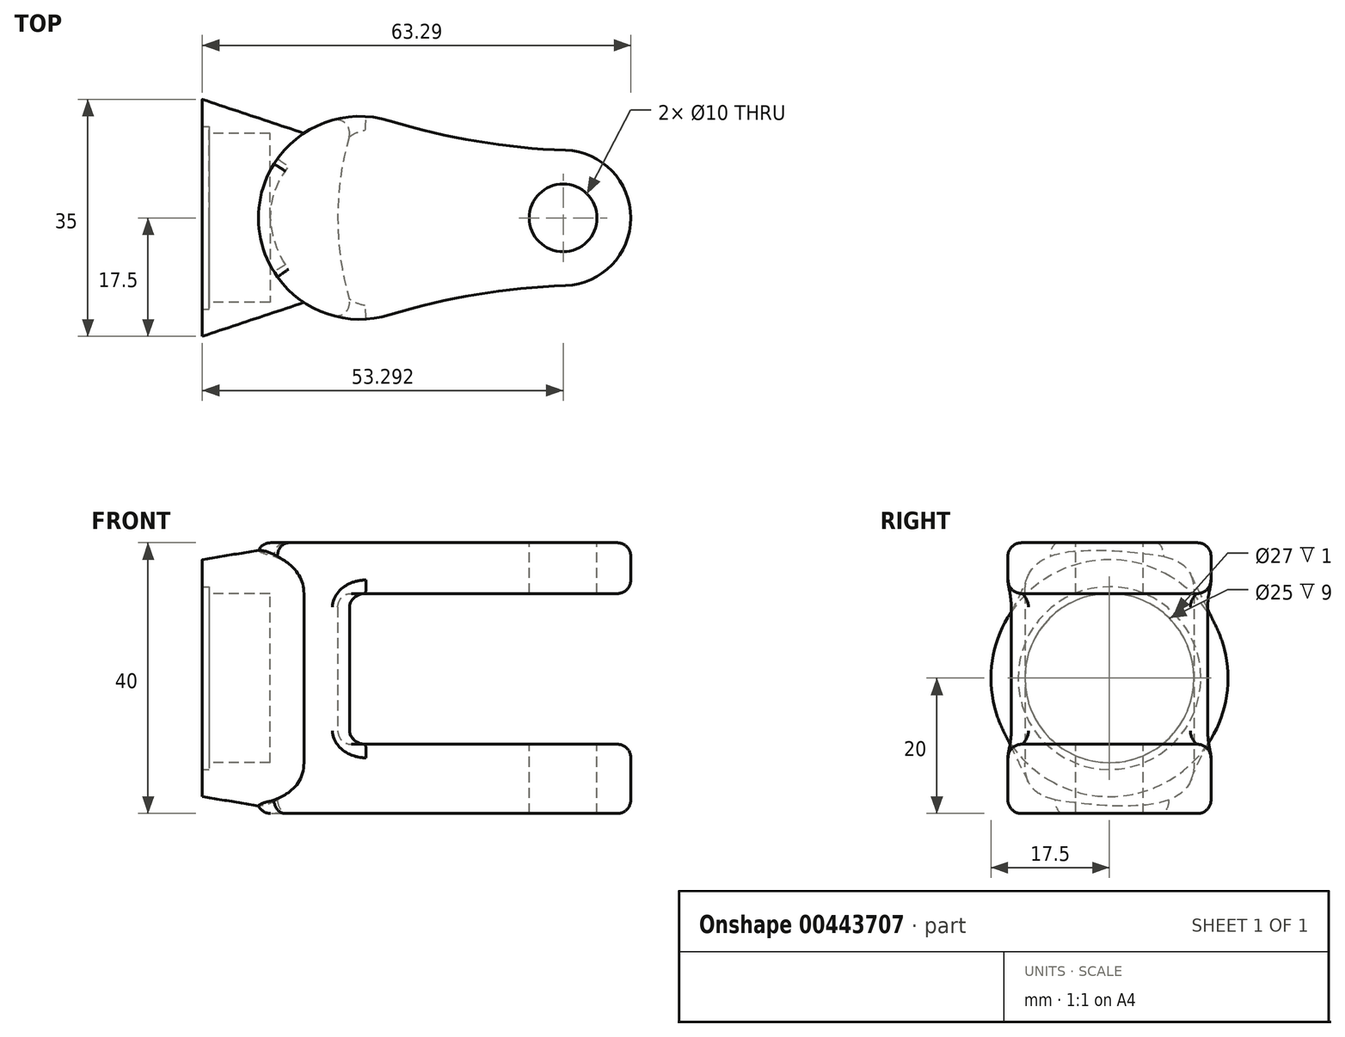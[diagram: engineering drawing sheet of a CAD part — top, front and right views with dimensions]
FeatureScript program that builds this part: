
annotation { "Feature Type Name" : "Feature", "Feature Type Description" : "" }
export const myFeature = defineFeature(function(context is Context, id is Id, definition is map)
    precondition{}
    {
        {
            var Q0;
            Q0=qCreatedBy(makeId("Right.planeOp"),FACE);
            var sketch = newSketch(context, id + "F0", { "sketchPlane" : qUnion([Q0])});
            skCircle(sketch, "E0", {"center": v(0, 0) * mm, "radius": 17.5 * mm});
            skSolve(sketch);
        }
        {
            var Q0;
            Q0=qCreatedBy(makeId("Right.planeOp"),FACE);
            cPlane(context, id + "F1", {"entities" : qUnion([Q0]), "cplaneType" : CPlaneType.OFFSET, "offset" : 15 * mm, "width" : 150 * mm, "height" : 150 * mm});
        }
        {
            var Q0;
            Q0=qCreatedBy(id+"F1.planeOp",FACE);
            var sketch = newSketch(context, id + "F2", { "sketchPlane" : qUnion([Q0])});
            skLineSegment(sketch, "E1.bottom", {"start": v(-5, 20) * mm, "end": v(5, 20) * mm});
            skLineSegment(sketch, "E1.top", {"start": v(-5, -20) * mm, "end": v(5, -20) * mm});
            skLineSegment(sketch, "E1.left", {"start": v(-12.5, 12.5) * mm, "end": v(-12.5, -12.5) * mm});
            skLineSegment(sketch, "E1.right", {"start": v(12.5, 12.5) * mm, "end": v(12.5, -12.5) * mm});
            skPoint(sketch, "E1.middle", {"position": v(0, 0) * mm});
            skPoint(sketch, "E2.visualSharp", {"position": v(-12.5, 20) * mm});
            skArc(sketch, "E2.filletArc", {"start": v(-5, 20) * mm, "mid": v(-10.3, 17.8) * mm, "end": v(-12.5, 12.5) * mm});
            skPoint(sketch, "E3.visualSharp", {"position": v(12.5, 20) * mm});
            skArc(sketch, "E3.filletArc", {"start": v(12.5, 12.5) * mm, "mid": v(10.3, 17.8) * mm, "end": v(5, 20) * mm});
            skPoint(sketch, "E4.visualSharp", {"position": v(-12.5, -20) * mm});
            skArc(sketch, "E4.filletArc", {"start": v(-12.5, -12.5) * mm, "mid": v(-10.3, -17.8) * mm, "end": v(-5, -20) * mm});
            skPoint(sketch, "E5.visualSharp", {"position": v(12.5, -20) * mm});
            skArc(sketch, "E5.filletArc", {"start": v(5, -20) * mm, "mid": v(10.3, -17.8) * mm, "end": v(12.5, -12.5) * mm});
            skSolve(sketch);
        }
        {
            var Q0;
            Q0=makeQuery(id+"F0.imprint","IMPRINT",FACE,{"disambiguationData":[TD([[makeQuery(id+"F0.imprint","IMPRINT",EDGE,{"derivedFrom":sQuery(id+"F0.wireOp",EDGE,"E0")}),1.0]])]});
            var Q1;
            Q1=makeQuery(id+"F2.imprint","IMPRINT",FACE,{"disambiguationData":[TD([[makeQuery(id+"F2.imprint","IMPRINT",EDGE,{"derivedFrom":sQuery(id+"F2.wireOp",EDGE,"E1.bottom")}),-1.0]])]});
            loft(context, id + "F3", {"sheetProfilesArray" : [{ "sheetProfileEntities" : qUnion([Q0]) }, { "sheetProfileEntities" : qUnion([Q1]) }]});
        }
        {
            var Q0;
            Q0=qCreatedBy(makeId("Top.planeOp"),FACE);
            var sketch = newSketch(context, id + "F4", { "sketchPlane" : qUnion([Q0])});
            skArc(sketch, "E6", {"start": v(27.7, 14.34) * mm, "mid": v(8.3, 0) * mm, "end": v(27.7, -14.34) * mm});
            skArc(sketch, "E7", {"start": v(53.63, -10) * mm, "mid": v(63.3, 0) * mm, "end": v(53.63, 10) * mm});
            skLineSegment(sketch, "E8", {"start": v(23.3, 0) * mm, "end": v(53.3, 0) * mm, "construction": true});
            skArc(sketch, "E9", {"start": v(53.63, -10) * mm, "mid": v(40.52, -11.31) * mm, "end": v(27.7, -14.34) * mm});
            skArc(sketch, "E10", {"start": v(27.7, 14.34) * mm, "mid": v(40.52, 11.31) * mm, "end": v(53.63, 10) * mm});
            skSolve(sketch);
        }
        {
            var Q0;
            Q0=makeQuery(id+"F4.imprint","IMPRINT",FACE,{"disambiguationData":[TD([[makeQuery(id+"F4.imprint","IMPRINT",EDGE,{"derivedFrom":sQuery(id+"F4.wireOp",EDGE,"E6")}),1.0]])]});
            extrude(context, id + "F5", {"entities" : qUnion([Q0]), "operationType" : NewBodyOperationType.ADD, "endBound" : BoundingType.SYMMETRIC, "depth" : 40 * mm});
        }
        {
            var Q0;
            Q0=qCreatedBy(makeId("Front.planeOp"),FACE);
            var sketch = newSketch(context, id + "F6", { "sketchPlane" : qUnion([Q0])});
            skLineSegment(sketch, "E11.bottom", {"start": v(20, 12.5) * mm, "end": v(63.63, 12.5) * mm});
            skLineSegment(sketch, "E11.top", {"start": v(20, -9.77) * mm, "end": v(63.63, -9.77) * mm});
            skLineSegment(sketch, "E11.left", {"start": v(20, 12.5) * mm, "end": v(20, -9.77) * mm});
            skLineSegment(sketch, "E11.right", {"start": v(63.63, 12.5) * mm, "end": v(63.63, -9.77) * mm});
            skSolve(sketch);
        }
        {
            var Q0;
            Q0 = qSketchRegion(id + "F6", true);
            var Q1;
            Q1=sQuery(id+"F6.wireOp",EDGE,"E11.right");
            revolve(context, id + "F7", {"operationType" : NewBodyOperationType.REMOVE, "entities" : qUnion([Q0]), "axis" : qUnion([Q1]), "revolveType" : RevolveType.FULL, "oppositeDirection" : true});
        }
        {
            var Q0;
            Q0=qCreatedBy(makeId("Right.planeOp"),FACE);
            var sketch = newSketch(context, id + "F8", { "sketchPlane" : qUnion([Q0])});
            skCircle(sketch, "E12", {"center": v(0, 0) * mm, "radius": 12.5 * mm});
            skSolve(sketch);
        }
        {
            var Q0;
            Q0 = qSketchRegion(id + "F8", true);
            extrude(context, id + "F9", {"entities" : qUnion([Q0]), "operationType" : NewBodyOperationType.REMOVE, "depth" : 10 * mm});
        }
        {
            var Q0;
            Q0=makeQuery(id+"F3.opLoft","CAP_FACE",FACE,{"disambiguationData":[OSD([makeQuery(id+"F0.imprint","IMPRINT",FACE,{"disambiguationData":[TD([[makeQuery(id+"F0.imprint","IMPRINT",EDGE,{"derivedFrom":sQuery(id+"F0.wireOp",EDGE,"E0")}),1.0]])]})])],"isStart":true});
            cPlane(context, id + "F10", {"entities" : qUnion([Q0]), "cplaneType" : CPlaneType.OFFSET, "offset" : 1 * mm, "oppositeDirection" : true, "width" : 150 * mm, "height" : 150 * mm});
        }
        {
            var Q0;
            Q0=qCreatedBy(id+"F10.planeOp",FACE);
            var sketch = newSketch(context, id + "F11", { "sketchPlane" : qUnion([Q0])});
            skCircle(sketch, "E13.0", {"center": v(0, 0) * mm, "radius": 13.5 * mm});
            skSolve(sketch);
        }
        {
            var Q0;
            Q0=makeQuery(id+"F11.imprint","IMPRINT",FACE,{"disambiguationData":[TD([[makeQuery(id+"F11.imprint","IMPRINT",EDGE,{"derivedFrom":sQuery(id+"F11.wireOp",EDGE,"E13.0")}),1.0]])]});
            var Q1;
            Q1=sQuery(id+"F11.wireOp",EDGE,"E13.0");
            extrude(context, id + "F12", {"entities" : qUnion([Q0]), "operationType" : NewBodyOperationType.REMOVE, "surfaceEntities" : qUnion([Q1]), "depth" : 1 * mm});
        }
        {
            var Q0;
            Q0=makeQuery(id+"F5.opExtrude","CAP_FACE",FACE,{"disambiguationData":[OSD([sQuery(id+"F4.wireOp",EDGE,"E6"),sQuery(id+"F4.wireOp",EDGE,"E7"),sQuery(id+"F4.wireOp",EDGE,"E9"),sQuery(id+"F4.wireOp",EDGE,"E10")])],"isStart":false});
            var sketch = newSketch(context, id + "F13", { "sketchPlane" : qUnion([Q0])});
            skCircle(sketch, "E14", {"center": v(53.3, 0) * mm, "radius": 5 * mm});
            skSolve(sketch);
        }
        {
            var Q0;
            Q0 = qSketchRegion(id + "F13", true);
            extrude(context, id + "F14", {"entities" : qUnion([Q0]), "operationType" : NewBodyOperationType.REMOVE, "endBound" : BoundingType.THROUGH_ALL, "oppositeDirection" : true, "depth" : 25 * mm});
        }
        {
            var Q0;
            Q0=makeQuery(id+"F7.boolean.opBoolean","COPY",EDGE,{"derivedFrom":makeQuery(id+"F7.opRevolve","SWEPT_EDGE",EDGE,{"disambiguationData":[OSD([sQuery(id+"F6.wireOp",EDGE,"E11.top"),sQuery(id+"F6.wireOp",EDGE,"E11.left")])]})});
            var Q1;
            Q1=makeQuery(id+"F7.boolean.opBoolean","COPY",EDGE,{"derivedFrom":makeQuery(id+"F7.opRevolve","SWEPT_EDGE",EDGE,{"disambiguationData":[OSD([sQuery(id+"F6.wireOp",EDGE,"E11.bottom"),sQuery(id+"F6.wireOp",EDGE,"E11.left")])]})});
            fillet(context, id + "F15", {"entities" : qUnion([Q0, Q1]), "radius" : 2 * mm, "tangentPropagation" : true, "allowEdgeOverflow" : false});
        }
        {
            var Q0;
            Q0=makeQuery(id+"F5.opExtrude","CAP_EDGE",EDGE,{"disambiguationData":[OSD([sQuery(id+"F4.wireOp",EDGE,"E7")])],"isStart":true});
            var Q1;
            Q1=makeQuery(id+"F5.opExtrude","CAP_EDGE",EDGE,{"disambiguationData":[OSD([sQuery(id+"F4.wireOp",EDGE,"E7")])],"isStart":false});
            var Q2;
            Q2=makeQuery(id+"F7.boolean.opBoolean","INTERSECT",EDGE,{"derivedFrom":[makeQuery(id+"F5.opExtrude","SWEPT_FACE",FACE,{"disambiguationData":[OSD([sQuery(id+"F4.wireOp",EDGE,"E7")])]}),makeQuery(id+"F7.opRevolve","SWEPT_FACE",FACE,{"disambiguationData":[OSD([sQuery(id+"F6.wireOp",EDGE,"E11.bottom")])]})]});
            var Q3;
            Q3=makeQuery(id+"F7.boolean.opBoolean","INTERSECT",EDGE,{"derivedFrom":[makeQuery(id+"F5.opExtrude","SWEPT_FACE",FACE,{"disambiguationData":[OSD([sQuery(id+"F4.wireOp",EDGE,"E7")])]}),makeQuery(id+"F7.opRevolve","SWEPT_FACE",FACE,{"disambiguationData":[OSD([sQuery(id+"F6.wireOp",EDGE,"E11.top")])]})]});
            fillet(context, id + "F16", {"entities" : qUnion([Q0, Q1, Q2, Q3]), "radius" : 2 * mm, "tangentPropagation" : true, "allowEdgeOverflow" : false});
        }
    });
